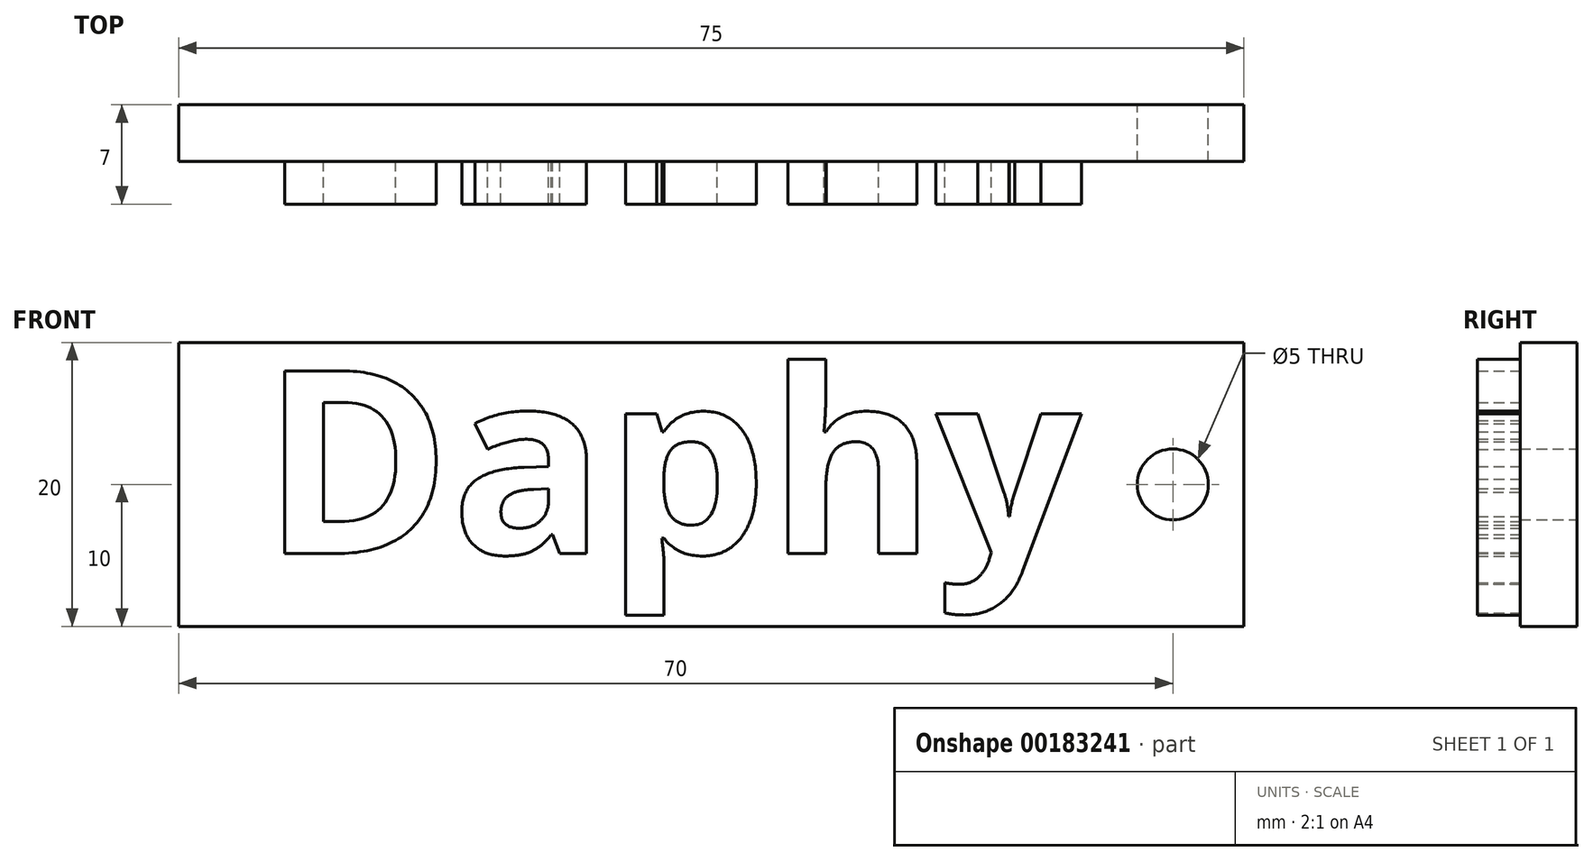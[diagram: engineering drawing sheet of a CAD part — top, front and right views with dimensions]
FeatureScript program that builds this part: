
annotation { "Feature Type Name" : "Feature", "Feature Type Description" : "" }
export const myFeature = defineFeature(function(context is Context, id is Id, definition is map)
    precondition{}
    {
        {
            var Q0;
            Q0=qCreatedBy(makeId("Front.planeOp"),FACE);
            var sketch = newSketch(context, id + "F0", { "sketchPlane" : qUnion([Q0])});
            skLineSegment(sketch, "E0.bottom", {"start": v(0, 0) * mm, "end": v(75, 0) * mm});
            skLineSegment(sketch, "E0.top", {"start": v(0, -20) * mm, "end": v(75, -20) * mm});
            skLineSegment(sketch, "E0.left", {"start": v(0, 0) * mm, "end": v(0, -20) * mm});
            skLineSegment(sketch, "E0.right", {"start": v(75, 0) * mm, "end": v(75, -20) * mm});
            skCircle(sketch, "E1", {"center": v(70, -10) * mm, "radius": 2.5 * mm});
            skSolve(sketch);
        }
        {
            var Q0;
            Q0=makeQuery(id+"F0.imprint","IMPRINT",FACE,{"disambiguationData":[TD([[makeQuery(id+"F0.imprint","IMPRINT",EDGE,{"derivedFrom":sQuery(id+"F0.wireOp",EDGE,"E0.bottom")}),-1.0]])]});
            extrude(context, id + "F1", {"entities" : qUnion([Q0]), "depth" : 4 * mm});
        }
        {
            var Q0;
            Q0=makeQuery(id+"F1.opExtrude","CAP_FACE",FACE,{"disambiguationData":[OSD([sQuery(id+"F0.wireOp",EDGE,"E0.bottom"),sQuery(id+"F0.wireOp",EDGE,"E0.top"),sQuery(id+"F0.wireOp",EDGE,"E0.left"),sQuery(id+"F0.wireOp",EDGE,"E0.right"),sQuery(id+"F0.wireOp",EDGE,"E1")])],"isStart":false});
            var sketch = newSketch(context, id + "F2", { "sketchPlane" : qUnion([Q0])});
            skText(sketch, "E2", { "text": "Daphy", "fontName": "OpenSans-Bold.ttf"});
            const initialGuessF2  = {"E2": [0.00583, -0.01487, 1, 0, 0.01298]};
            skSetInitialGuess(sketch, initialGuessF2);
            skSolve(sketch);
        }
        {
            var Q0;
            Q0 = qSketchRegion(id + "F2", true);
            extrude(context, id + "F3", {"entities" : qUnion([Q0]), "operationType" : NewBodyOperationType.ADD, "depth" : 3 * mm});
        }
    });
